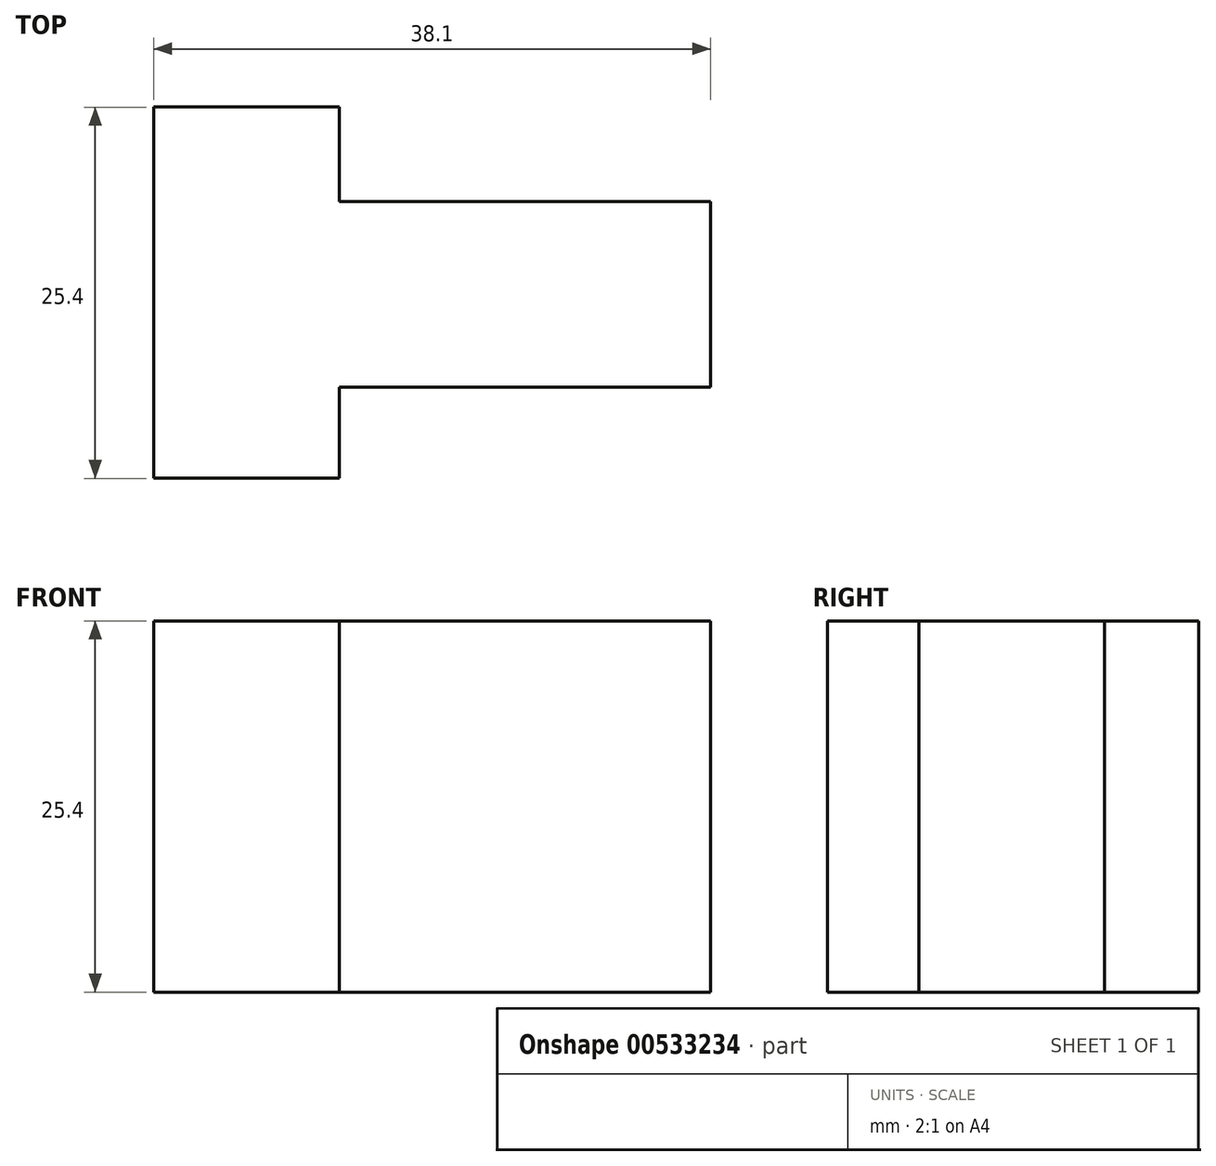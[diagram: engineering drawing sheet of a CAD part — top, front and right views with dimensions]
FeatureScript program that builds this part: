
annotation { "Feature Type Name" : "Feature", "Feature Type Description" : "" }
export const myFeature = defineFeature(function(context is Context, id is Id, definition is map)
    precondition{}
    {
        {
            var Q0;
            Q0=qCreatedBy(makeId("Top.planeOp"),FACE);
            var sketch = newSketch(context, id + "F0", { "sketchPlane" : qUnion([Q0])});
            skLineSegment(sketch, "E0", {"start": v(-52.53, 16.64) * mm, "end": v(-52.53, 42.04) * mm});
            skLineSegment(sketch, "E1", {"start": v(-52.53, 42.04) * mm, "end": v(-39.83, 42.04) * mm});
            skLineSegment(sketch, "E2", {"start": v(-52.53, 16.64) * mm, "end": v(-39.83, 16.64) * mm});
            skLineSegment(sketch, "E3", {"start": v(-39.83, 42.04) * mm, "end": v(-39.83, 35.6) * mm});
            skLineSegment(sketch, "E4", {"start": v(-39.83, 16.64) * mm, "end": v(-39.83, 22.9) * mm});
            skLineSegment(sketch, "E5", {"start": v(-39.83, 22.9) * mm, "end": v(-14.43, 22.9) * mm});
            skLineSegment(sketch, "E6", {"start": v(-39.83, 35.6) * mm, "end": v(-14.43, 35.6) * mm});
            skLineSegment(sketch, "E7", {"start": v(-14.43, 35.6) * mm, "end": v(-14.43, 22.9) * mm});
            skSolve(sketch);
        }
        {
            var Q0;
            Q0 = qSketchRegion(id + "F0", true);
            extrude(context, id + "F1", {"entities" : qUnion([Q0]), "depth" : 25.4 * mm, "offsetDistance" : 25.4 * mm});
        }
    });
